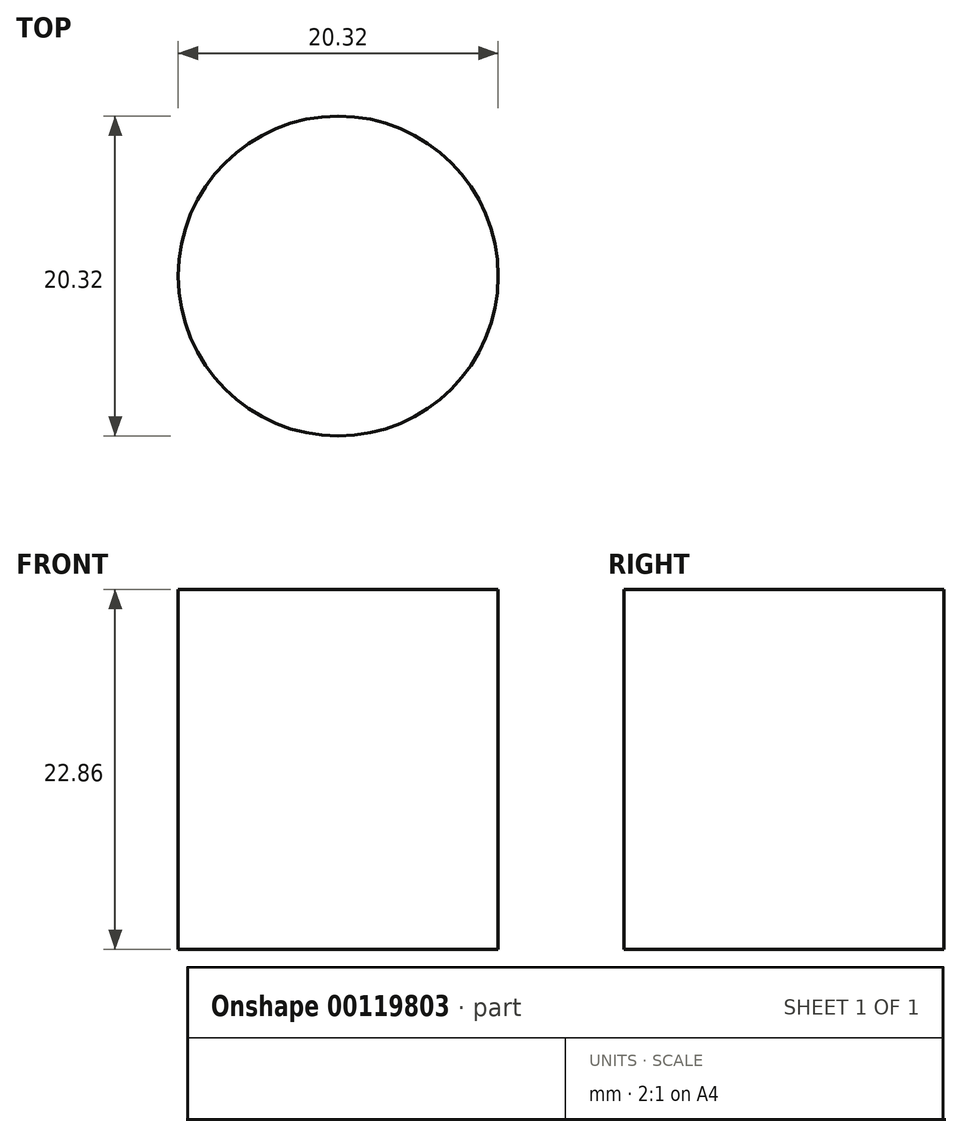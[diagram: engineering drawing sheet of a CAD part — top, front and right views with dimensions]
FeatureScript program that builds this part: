
annotation { "Feature Type Name" : "Feature", "Feature Type Description" : "" }
export const myFeature = defineFeature(function(context is Context, id is Id, definition is map)
    precondition{}
    {
        {
            var Q0;
            Q0=qCreatedBy(makeId("Top.planeOp"),FACE);
            var sketch = newSketch(context, id + "F0", { "sketchPlane" : qUnion([Q0])});
            skCircle(sketch, "E0", {"center": v(-56.89, 36.85) * mm, "radius": 10.16 * mm});
            skSolve(sketch);
        }
        {
            var Q0;
            Q0=makeQuery(id+"F0.imprint","IMPRINT",FACE,{"disambiguationData":[TD([[makeQuery(id+"F0.imprint","IMPRINT",EDGE,{"derivedFrom":sQuery(id+"F0.wireOp",EDGE,"E0")}),1.0]])]});
            extrude(context, id + "F1", {"entities" : qUnion([Q0]), "depth" : 22.86 * mm});
        }
    });
